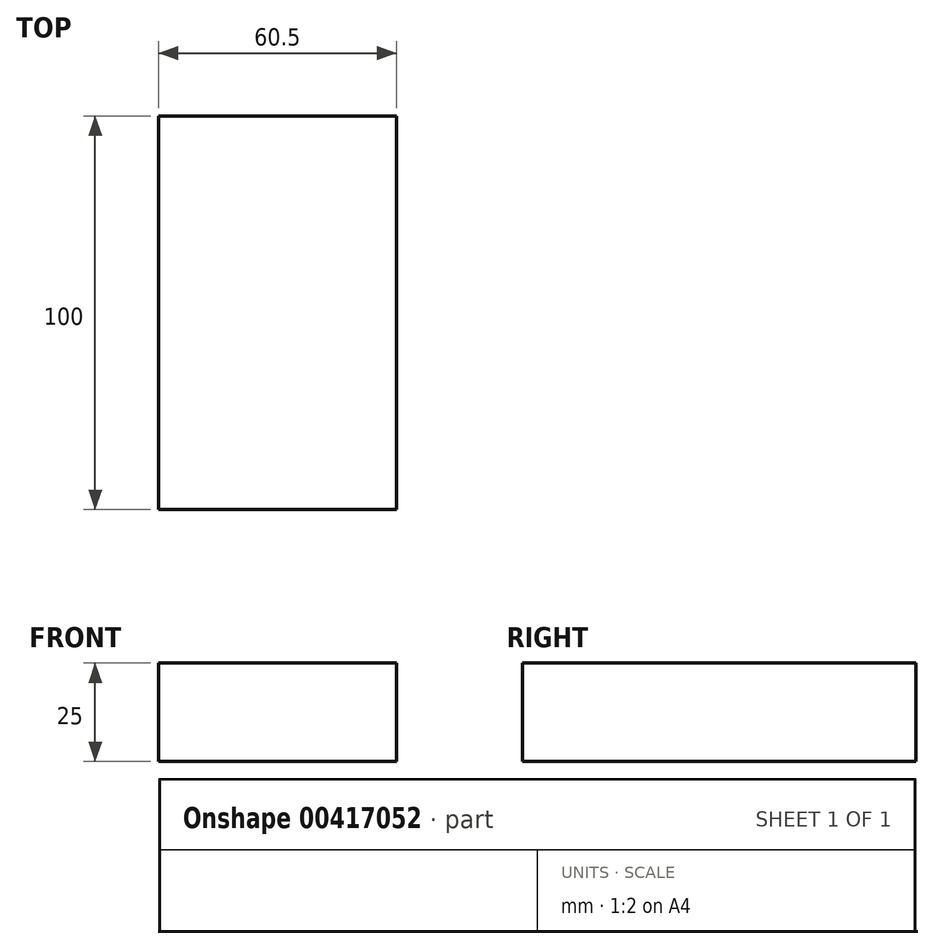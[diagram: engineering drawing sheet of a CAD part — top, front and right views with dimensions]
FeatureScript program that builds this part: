
annotation { "Feature Type Name" : "Feature", "Feature Type Description" : "" }
export const myFeature = defineFeature(function(context is Context, id is Id, definition is map)
    precondition{}
    {
        {
            var Q0;
            Q0=qCreatedBy(makeId("Front.planeOp"),FACE);
            var sketch = newSketch(context, id + "F0", { "sketchPlane" : qUnion([Q0])});
            skLineSegment(sketch, "E0.bottom", {"start": v(-30.25, -12.5) * mm, "end": v(30.25, -12.5) * mm});
            skLineSegment(sketch, "E0.top", {"start": v(-30.25, 12.5) * mm, "end": v(30.25, 12.5) * mm});
            skLineSegment(sketch, "E0.left", {"start": v(-30.25, -12.5) * mm, "end": v(-30.25, 12.5) * mm});
            skLineSegment(sketch, "E0.right", {"start": v(30.25, -12.5) * mm, "end": v(30.25, 12.5) * mm});
            skPoint(sketch, "E0.middle", {"position": v(0, 0) * mm});
            skLineSegment(sketch, "E1.bottom", {"start": v(57.2, 30.56) * mm, "end": v(82.2, 30.56) * mm});
            skLineSegment(sketch, "E1.top", {"start": v(57.2, 55.56) * mm, "end": v(82.2, 55.56) * mm});
            skLineSegment(sketch, "E1.left", {"start": v(57.2, 30.56) * mm, "end": v(57.2, 55.56) * mm});
            skLineSegment(sketch, "E1.right", {"start": v(82.2, 30.56) * mm, "end": v(82.2, 55.56) * mm});
            skPoint(sketch, "E1.middle", {"position": v(69.7, 43.06) * mm});
            skLineSegment(sketch, "E2", {"start": v(30.25, 12.5) * mm, "end": v(30.25, 27.47) * mm});
            skArc(sketch, "E3", {"start": v(30.25, 27.47) * mm, "mid": v(34.94, 38.78) * mm, "end": v(46.25, 43.47) * mm});
            skLineSegment(sketch, "E4", {"start": v(46.25, 43.47) * mm, "end": v(69.25, 43.47) * mm});
            skLineSegment(sketch, "E5.0", {"start": v(46.25, 50.97) * mm, "end": v(69.25, 50.97) * mm});
            skArc(sketch, "E5.1", {"start": v(22.75, 27.47) * mm, "mid": v(29.63, 44.08) * mm, "end": v(46.25, 50.97) * mm});
            skLineSegment(sketch, "E5.2", {"start": v(22.75, 12.5) * mm, "end": v(22.75, 27.47) * mm});
            skLineSegment(sketch, "E6", {"start": v(69.25, 50.97) * mm, "end": v(69.7, 43.06) * mm});
            skFitSpline(sketch, "E7", {"points": [v(-30.25, 12.5) * mm, v(46.25, 50.97) * mm], "startDerivative": vector(41.84, 98.26) * mm, "endDerivative": vector(89, -13.21) * mm});
            skSolve(sketch);
        }
        {
            var Q0;
            Q0=makeQuery(id+"F0.imprint","IMPRINT",FACE,{"disambiguationData":[TD([[makeQuery(id+"F0.imprint","IMPRINT",EDGE,{"derivedFrom":sQuery(id+"F0.wireOp",EDGE,"E0.bottom")}),1.0]])]});
            extrude(context, id + "F1", {"entities" : qUnion([Q0]), "endBound" : BoundingType.SYMMETRIC, "depth" : 100 * mm});
        }
    });
